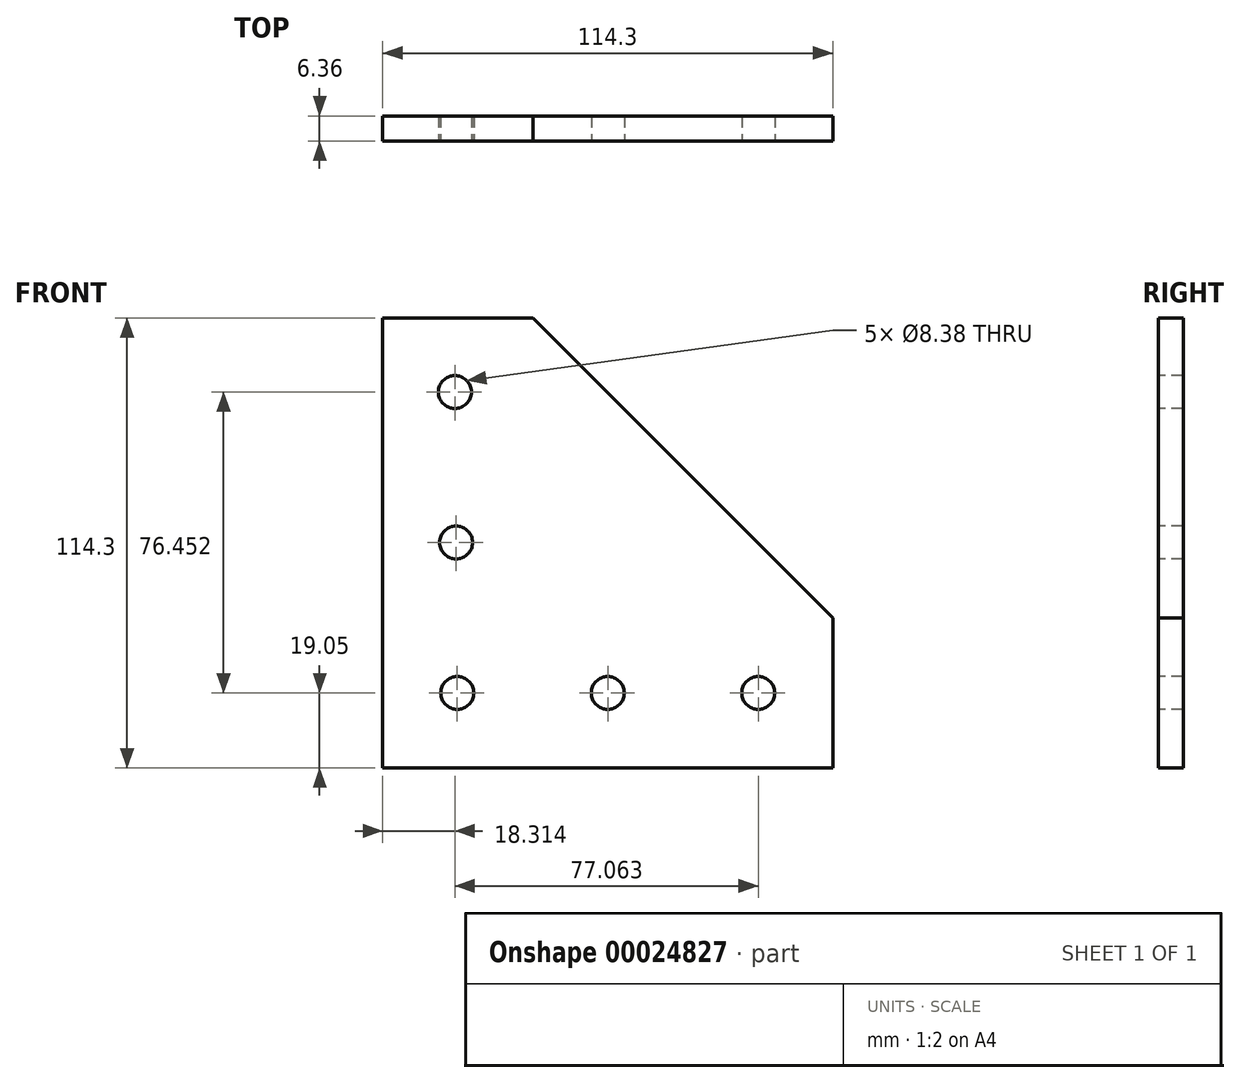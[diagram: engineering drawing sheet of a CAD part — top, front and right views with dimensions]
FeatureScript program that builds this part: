
annotation { "Feature Type Name" : "Feature", "Feature Type Description" : "" }
export const myFeature = defineFeature(function(context is Context, id is Id, definition is map)
    precondition{}
    {
        {
            var Q0;
            Q0=qCreatedBy(makeId("Front.planeOp"),FACE);
            var sketch = newSketch(context, id + "F0", { "sketchPlane" : qUnion([Q0])});
            skLineSegment(sketch, "E0.rect.bottom", {"start": v(-19.05, 57.15) * mm, "end": v(-57.15, 57.15) * mm});
            skLineSegment(sketch, "E0.rect.top", {"start": v(57.15, -57.15) * mm, "end": v(-57.15, -57.15) * mm});
            skLineSegment(sketch, "E0.rect.left", {"start": v(57.15, -19.05) * mm, "end": v(57.15, -57.15) * mm});
            skLineSegment(sketch, "E0.rect.right", {"start": v(-57.15, 57.15) * mm, "end": v(-57.15, -57.15) * mm});
            skPoint(sketch, "E0.rect.middle", {"position": v(0, 0) * mm});
            skLineSegment(sketch, "E1", {"start": v(-19.05, 57.15) * mm, "end": v(57.15, -19.05) * mm});
            skPoint(sketch, "E2.orphan", {"position": v(57.15, 57.15) * mm});
            skSolve(sketch);
        }
        {
            var Q0;
            Q0=makeQuery(id+"F0.imprint","IMPRINT",FACE,{"disambiguationData":[TD([[makeQuery(id+"F0.imprint","IMPRINT",EDGE,{"derivedFrom":sQuery(id+"F0.wireOp",EDGE,"E0.rect.bottom")}),1.0]])]});
            extrude(context, id + "F1", {"entities" : qUnion([Q0]), "endBound" : BoundingType.SYMMETRIC, "depth" : 6.35 * mm});
        }
        {
            var Q0;
            Q0=makeQuery(id+"F1.opExtrude","CAP_FACE",FACE,{"disambiguationData":[OSD([sQuery(id+"F0.wireOp",EDGE,"E0.rect.bottom"),sQuery(id+"F0.wireOp",EDGE,"E0.rect.top"),sQuery(id+"F0.wireOp",EDGE,"E0.rect.left"),sQuery(id+"F0.wireOp",EDGE,"E0.rect.right"),sQuery(id+"F0.wireOp",EDGE,"E1")])],"isStart":false});
            var sketch = newSketch(context, id + "F2", { "sketchPlane" : qUnion([Q0])});
            skCircle(sketch, "E3", {"center": v(38.23, -38.1) * mm, "radius": 4.2 * mm});
            skCircle(sketch, "E4.1.0.0", {"center": v(0, -38.1) * mm, "radius": 4.2 * mm});
            skCircle(sketch, "E4.2.0.0", {"center": v(-38.23, -38.1) * mm, "radius": 4.2 * mm});
            skLineSegment(sketch, "E4.direction1", {"start": v(38.23, -38.1) * mm, "end": v(0, -38.1) * mm, "construction": true});
            skCircle(sketch, "E5.1.0.0", {"center": v(-38.53, 0.13) * mm, "radius": 4.2 * mm});
            skCircle(sketch, "E5.2.0.0", {"center": v(-38.84, 38.35) * mm, "radius": 4.2 * mm});
            skLineSegment(sketch, "E5.direction1", {"start": v(-38.23, -38.1) * mm, "end": v(-38.53, 0.13) * mm, "construction": true});
            skSolve(sketch);
        }
        {
            var Q0;
            Q0 = qSketchRegion(id + "F2", true);
            var Q1;
            Q1 = qBodyType(qCreatedBy(id + "F2" ,EDGE), BodyType.WIRE);
            extrude(context, id + "F3", {"entities" : qUnion([Q0]), "operationType" : NewBodyOperationType.REMOVE, "surfaceEntities" : qUnion([Q1]), "endBound" : BoundingType.THROUGH_ALL, "oppositeDirection" : true, "depth" : 25.4 * mm});
        }
    });
